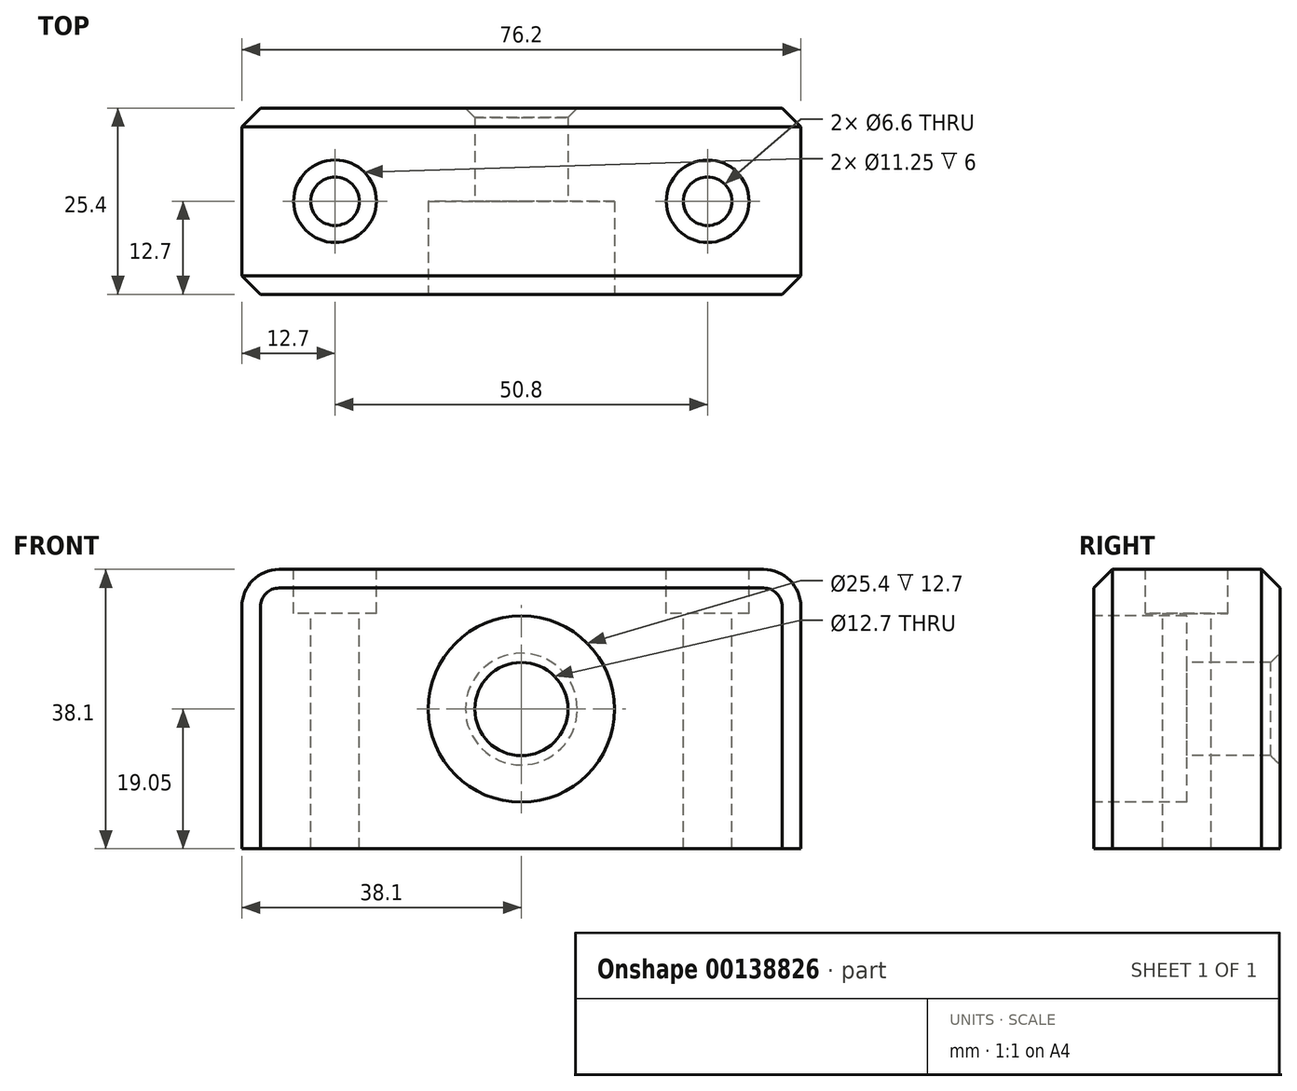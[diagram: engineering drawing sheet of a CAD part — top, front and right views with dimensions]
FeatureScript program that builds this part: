
annotation { "Feature Type Name" : "Feature", "Feature Type Description" : "" }
export const myFeature = defineFeature(function(context is Context, id is Id, definition is map)
    precondition{}
    {
        {
            var Q0;
            Q0=qCreatedBy(makeId("Front.planeOp"),FACE);
            var sketch = newSketch(context, id + "F0", { "sketchPlane" : qUnion([Q0])});
            skLineSegment(sketch, "E0.bottom", {"start": v(0, 0) * mm, "end": v(76.2, 0) * mm});
            skLineSegment(sketch, "E0.top", {"start": v(0, 38.1) * mm, "end": v(76.2, 38.1) * mm});
            skLineSegment(sketch, "E0.left", {"start": v(0, 0) * mm, "end": v(0, 38.1) * mm});
            skLineSegment(sketch, "E0.right", {"start": v(76.2, 0) * mm, "end": v(76.2, 38.1) * mm});
            skSolve(sketch);
        }
        {
            var Q0;
            Q0 = qSketchRegion(id + "F0", true);
            extrude(context, id + "F1", {"entities" : qUnion([Q0]), "depth" : 25.4 * mm});
        }
        {
            var Q0;
            Q0=makeQuery(id+"F1.opExtrude","SWEPT_EDGE",EDGE,{"disambiguationData":[OSD([sQuery(id+"F0.wireOp",EDGE,"E0.top"),sQuery(id+"F0.wireOp",EDGE,"E0.right")])]});
            var Q1;
            Q1=makeQuery(id+"F1.opExtrude","SWEPT_EDGE",EDGE,{"disambiguationData":[OSD([sQuery(id+"F0.wireOp",EDGE,"E0.top"),sQuery(id+"F0.wireOp",EDGE,"E0.left")])]});
            fillet(context, id + "F2", {"entities" : qUnion([Q0, Q1]), "radius" : 5.08 * mm, "tangentPropagation" : true, "allowEdgeOverflow" : false});
        }
        {
            var Q0;
            Q0=makeQuery(id+"F1.opExtrude","CAP_FACE",FACE,{"disambiguationData":[OSD([sQuery(id+"F0.wireOp",EDGE,"E0.bottom"),sQuery(id+"F0.wireOp",EDGE,"E0.top"),sQuery(id+"F0.wireOp",EDGE,"E0.left"),sQuery(id+"F0.wireOp",EDGE,"E0.right")])],"isStart":false});
            var sketch = newSketch(context, id + "F3", { "sketchPlane" : qUnion([Q0])});
            skCircle(sketch, "E1", {"center": v(38.1, 19.05) * mm, "radius": 12.7 * mm});
            skLineSegment(sketch, "E2", {"start": v(38.1, 38.1) * mm, "end": v(38.1, 0) * mm, "construction": true});
            skSolve(sketch);
        }
        {
            var Q0;
            Q0=makeQuery(id+"F3.imprint","IMPRINT",FACE,{"disambiguationData":[TD([[makeQuery(id+"F3.imprint","IMPRINT",EDGE,{"derivedFrom":sQuery(id+"F3.wireOp",EDGE,"E1")}),1.0]])]});
            var Q1;
            Q1=sQuery(id+"F3.wireOp",EDGE,"E1");
            extrude(context, id + "F4", {"entities" : qUnion([Q0]), "operationType" : NewBodyOperationType.REMOVE, "surfaceEntities" : qUnion([Q1]), "oppositeDirection" : true, "depth" : 12.7 * mm});
        }
        {
            var Q0;
            Q0=makeQuery(id+"F4.boolean.opBoolean","COPY",FACE,{"derivedFrom":makeQuery(id+"F4.opExtrude","CAP_FACE",FACE,{"disambiguationData":[OSD([sQuery(id+"F3.wireOp",EDGE,"E1")])],"isStart":false})});
            var sketch = newSketch(context, id + "F5", { "sketchPlane" : qUnion([Q0])});
            skCircle(sketch, "E3", {"center": v(38.1, 19.05) * mm, "radius": 6.35 * mm});
            skSolve(sketch);
        }
        {
            var Q0;
            Q0 = qSketchRegion(id + "F5", true);
            extrude(context, id + "F6", {"entities" : qUnion([Q0]), "operationType" : NewBodyOperationType.REMOVE, "endBound" : BoundingType.THROUGH_ALL, "oppositeDirection" : true, "depth" : 25.4 * mm});
        }
        {
            var Q0;
            Q0=makeQuery(id+"F1.opExtrude","SWEPT_FACE",FACE,{"disambiguationData":[OSD([sQuery(id+"F0.wireOp",EDGE,"E0.top")])]});
            var sketch = newSketch(context, id + "F7", { "sketchPlane" : qUnion([Q0])});
            skPoint(sketch, "E4", {"position": v(12.7, -12.7) * mm});
            skPoint(sketch, "E5", {"position": v(63.5, -12.7) * mm});
            skLineSegment(sketch, "E6", {"start": v(5.08, -12.7) * mm, "end": v(71.12, -12.7) * mm, "construction": true});
            skSolve(sketch);
        }
        {
            var Q0;
            Q0=sQuery(id+"F7.wireOp",VERTEX,"E4");
            var Q1;
            Q1=sQuery(id+"F7.wireOp",VERTEX,"E5");
            var Q2;
            Q2=makeQuery(id+"F1.opExtrude","SWEPT_BODY",BODY,{"disambiguationData":[OSD([sQuery(id+"F0.wireOp",EDGE,"E0.bottom"),sQuery(id+"F0.wireOp",EDGE,"E0.top"),sQuery(id+"F0.wireOp",EDGE,"E0.left"),sQuery(id+"F0.wireOp",EDGE,"E0.right")])]});
            hole(context, id + "F8", {"style" : HoleStyle.C_BORE, "endStyle" : HoleEndStyle.THROUGH, "standardTappedOrClearance" : lookupTablePath({ "standard" : "ISO", "fit" : "Normal", "size" : "M6", "type" : "Clearance" }), "standardBlindInLast" : lookupTablePath({ "fit" : "Standard", "standard" : "ISO", "size" : "M6", "type" : "Clearance" }), "holeDiameter" : 6.6 * mm, "cBoreDiameter" : 11.25 * mm, "cBoreDepth" : 6 * mm, "locations" : qUnion([Q0, Q1]), "scope" : qUnion([Q2]), "isTappedThrough" : true});
        }
        {
            var Q0;
            Q0=makeQuery(id+"F1.opExtrude","CAP_EDGE",EDGE,{"disambiguationData":[OSD([sQuery(id+"F0.wireOp",EDGE,"E0.top")])],"isStart":false});
            var Q1;
            Q1=makeQuery(id+"F1.opExtrude","CAP_EDGE",EDGE,{"disambiguationData":[OSD([sQuery(id+"F0.wireOp",EDGE,"E0.top")])],"isStart":true});
            chamfer(context, id + "F9", {"entities" : qUnion([Q0, Q1]), "width" : 2.54 * mm, "tangentPropagation" : true});
        }
        {
            var Q0;
            Q0=makeQuery(id+"F6.boolean.opBoolean","INTERSECT",EDGE,{"derivedFrom":[makeQuery(id+"F1.opExtrude","CAP_FACE",FACE,{"disambiguationData":[OSD([sQuery(id+"F0.wireOp",EDGE,"E0.bottom"),sQuery(id+"F0.wireOp",EDGE,"E0.top"),sQuery(id+"F0.wireOp",EDGE,"E0.left"),sQuery(id+"F0.wireOp",EDGE,"E0.right")])],"isStart":true}),makeQuery(id+"F6.opExtrude","SWEPT_FACE",FACE,{"disambiguationData":[OSD([sQuery(id+"F5.wireOp",EDGE,"E3")])]})]});
            var Q1;
            Q1=makeQuery(id+"F6.boolean.opBoolean","COPY",EDGE,{"derivedFrom":makeQuery(id+"F6.opExtrude","CAP_EDGE",EDGE,{"disambiguationData":[OSD([sQuery(id+"F5.wireOp",EDGE,"E3")])],"isStart":true})});
            var Q2;
            Q2=makeQuery(id+"F4.boolean.opBoolean","COPY",EDGE,{"derivedFrom":makeQuery(id+"F4.opExtrude","CAP_EDGE",EDGE,{"disambiguationData":[OSD([sQuery(id+"F3.wireOp",EDGE,"E1")])],"isStart":true})});
            chamfer(context, id + "F10", {"entities" : qUnion([Q0, Q1, Q2]), "width" : 1.27 * mm, "tangentPropagation" : true});
        }
    });
